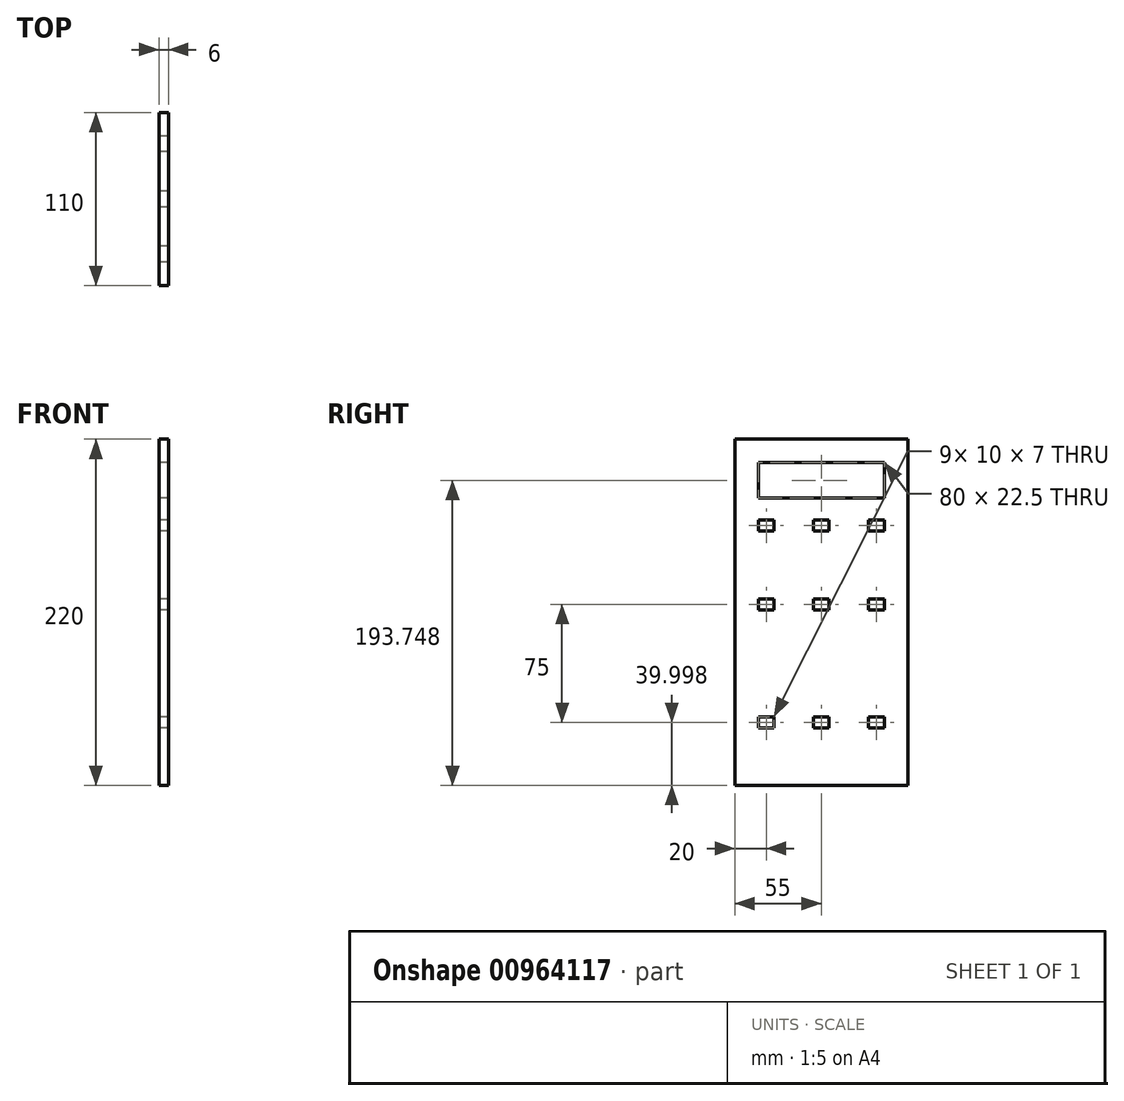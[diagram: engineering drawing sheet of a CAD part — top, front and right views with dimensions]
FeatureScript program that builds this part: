
annotation { "Feature Type Name" : "Feature", "Feature Type Description" : "" }
export const myFeature = defineFeature(function(context is Context, id is Id, definition is map)
    precondition{}
    {
        {
            var Q0;
            Q0=qCreatedBy(makeId("Right.planeOp"),FACE);
            var sketch = newSketch(context, id + "F0", { "sketchPlane" : qUnion([Q0])});
            skLineSegment(sketch, "E0.bottom", {"start": v(-47.5, 157.22) * mm, "end": v(62.5, 157.22) * mm});
            skLineSegment(sketch, "E0.top", {"start": v(-47.5, -62.78) * mm, "end": v(62.5, -62.78) * mm});
            skLineSegment(sketch, "E0.left", {"start": v(-47.5, 157.22) * mm, "end": v(-47.5, -62.78) * mm});
            skLineSegment(sketch, "E0.right", {"start": v(62.5, 157.22) * mm, "end": v(62.5, -62.78) * mm});
            skLineSegment(sketch, "E1.bottom", {"start": v(37.5, -19.28) * mm, "end": v(47.5, -19.28) * mm});
            skLineSegment(sketch, "E1.top", {"start": v(37.5, -26.28) * mm, "end": v(47.5, -26.28) * mm});
            skLineSegment(sketch, "E1.left", {"start": v(37.5, -19.28) * mm, "end": v(37.5, -26.28) * mm});
            skLineSegment(sketch, "E1.right", {"start": v(47.5, -19.28) * mm, "end": v(47.5, -26.28) * mm});
            skPoint(sketch, "E1.middle", {"position": v(42.5, -22.78) * mm});
            skLineSegment(sketch, "E2.bottom", {"start": v(2.5, -19.28) * mm, "end": v(12.5, -19.28) * mm});
            skLineSegment(sketch, "E2.top", {"start": v(2.5, -26.28) * mm, "end": v(12.5, -26.28) * mm});
            skLineSegment(sketch, "E2.left", {"start": v(2.5, -19.28) * mm, "end": v(2.5, -26.28) * mm});
            skLineSegment(sketch, "E2.right", {"start": v(12.5, -19.28) * mm, "end": v(12.5, -26.28) * mm});
            skPoint(sketch, "E2.middle", {"position": v(7.5, -22.78) * mm});
            skLineSegment(sketch, "E3.bottom", {"start": v(-22.5, -19.28) * mm, "end": v(-32.5, -19.28) * mm});
            skLineSegment(sketch, "E3.top", {"start": v(-22.5, -26.28) * mm, "end": v(-32.5, -26.28) * mm});
            skLineSegment(sketch, "E3.left", {"start": v(-22.5, -19.28) * mm, "end": v(-22.5, -26.28) * mm});
            skLineSegment(sketch, "E3.right", {"start": v(-32.5, -19.28) * mm, "end": v(-32.5, -26.28) * mm});
            skPoint(sketch, "E3.middle", {"position": v(-27.5, -22.78) * mm});
            skLineSegment(sketch, "E4", {"start": v(-27.5, -22.78) * mm, "end": v(42.5, -22.78) * mm});
            skLineSegment(sketch, "E5", {"start": v(-47.5, 130.37) * mm, "end": v(-32.5, 130.37) * mm});
            skLineSegment(sketch, "E6", {"start": v(62.5, 129.84) * mm, "end": v(47.5, 129.84) * mm});
            skLineSegment(sketch, "E7", {"start": v(9.43, 157.22) * mm, "end": v(9.43, 142.22) * mm});
            skLineSegment(sketch, "E8", {"start": v(9.43, 142.22) * mm, "end": v(-32.5, 142.22) * mm});
            skLineSegment(sketch, "E9", {"start": v(-32.5, 142.22) * mm, "end": v(-32.5, 119.72) * mm});
            skLineSegment(sketch, "E10", {"start": v(-32.5, 119.72) * mm, "end": v(47.5, 119.72) * mm});
            skLineSegment(sketch, "E11", {"start": v(47.5, 119.72) * mm, "end": v(47.5, 142.22) * mm});
            skLineSegment(sketch, "E12", {"start": v(47.5, 142.22) * mm, "end": v(9.43, 142.22) * mm});
            skLineSegment(sketch, "E13", {"start": v(30.25, -22.78) * mm, "end": v(30.25, 14.72) * mm});
            skLineSegment(sketch, "E14", {"start": v(30.25, 14.72) * mm, "end": v(-3.72, 14.72) * mm});
            skLineSegment(sketch, "E15.MirrorCS", {"start": v(37.5, 55.72) * mm, "end": v(47.5, 55.72) * mm});
            skLineSegment(sketch, "E16.MirrorCS", {"start": v(-32.5, 48.72) * mm, "end": v(-32.5, 55.72) * mm});
            skLineSegment(sketch, "E17.MirrorCS", {"start": v(37.5, 48.72) * mm, "end": v(37.5, 55.72) * mm});
            skLineSegment(sketch, "E18.MirrorCS", {"start": v(-22.5, 55.72) * mm, "end": v(-32.5, 55.72) * mm});
            skLineSegment(sketch, "E19.MirrorCS", {"start": v(2.5, 48.72) * mm, "end": v(2.5, 55.72) * mm});
            skLineSegment(sketch, "E20.MirrorCS", {"start": v(2.5, 55.72) * mm, "end": v(12.5, 55.72) * mm});
            skLineSegment(sketch, "E21.MirrorCS", {"start": v(37.5, 48.72) * mm, "end": v(47.5, 48.72) * mm});
            skLineSegment(sketch, "E22.MirrorCS", {"start": v(2.5, 48.72) * mm, "end": v(12.5, 48.72) * mm});
            skLineSegment(sketch, "E23.MirrorCS", {"start": v(-22.5, 48.72) * mm, "end": v(-22.5, 55.72) * mm});
            skLineSegment(sketch, "E24.MirrorCS", {"start": v(-22.5, 48.72) * mm, "end": v(-32.5, 48.72) * mm});
            skPoint(sketch, "E25.MirrorP", {"position": v(7.5, 52.22) * mm});
            skPoint(sketch, "E26.MirrorP", {"position": v(-27.5, 52.22) * mm});
            skPoint(sketch, "E27.MirrorP", {"position": v(42.5, 52.22) * mm});
            skLineSegment(sketch, "E28.MirrorCS", {"start": v(47.5, 48.72) * mm, "end": v(47.5, 55.72) * mm});
            skLineSegment(sketch, "E29.MirrorCS", {"start": v(-27.5, 52.22) * mm, "end": v(42.5, 52.22) * mm});
            skLineSegment(sketch, "E30.MirrorCS", {"start": v(12.5, 48.72) * mm, "end": v(12.5, 55.72) * mm});
            skLineSegment(sketch, "E31", {"start": v(24, 52.22) * mm, "end": v(24, 77.22) * mm});
            skLineSegment(sketch, "E32", {"start": v(24, 77.22) * mm, "end": v(-2.6, 77.22) * mm});
            skLineSegment(sketch, "E33.MirrorCS", {"start": v(-22.5, 98.72) * mm, "end": v(-32.5, 98.72) * mm});
            skLineSegment(sketch, "E34.MirrorCS", {"start": v(12.5, 105.72) * mm, "end": v(12.5, 98.72) * mm});
            skLineSegment(sketch, "E35.MirrorCS", {"start": v(37.5, 98.72) * mm, "end": v(47.5, 98.72) * mm});
            skLineSegment(sketch, "E36.MirrorCS", {"start": v(2.5, 98.72) * mm, "end": v(12.5, 98.72) * mm});
            skLineSegment(sketch, "E37.MirrorCS", {"start": v(2.5, 105.72) * mm, "end": v(12.5, 105.72) * mm});
            skLineSegment(sketch, "E38.MirrorCS", {"start": v(37.5, 105.72) * mm, "end": v(47.5, 105.72) * mm});
            skLineSegment(sketch, "E39.MirrorCS", {"start": v(-22.5, 105.72) * mm, "end": v(-22.5, 98.72) * mm});
            skPoint(sketch, "E40.MirrorP", {"position": v(42.5, 102.22) * mm});
            skLineSegment(sketch, "E41.MirrorCS", {"start": v(2.5, 105.72) * mm, "end": v(2.5, 98.72) * mm});
            skLineSegment(sketch, "E42.MirrorCS", {"start": v(47.5, 105.72) * mm, "end": v(47.5, 98.72) * mm});
            skLineSegment(sketch, "E43.MirrorCS", {"start": v(-32.5, 105.72) * mm, "end": v(-32.5, 98.72) * mm});
            skPoint(sketch, "E44.MirrorP", {"position": v(7.5, 102.22) * mm});
            skPoint(sketch, "E45.MirrorP", {"position": v(-27.5, 102.22) * mm});
            skLineSegment(sketch, "E46.MirrorCS", {"start": v(37.5, 105.72) * mm, "end": v(37.5, 98.72) * mm});
            skLineSegment(sketch, "E47.MirrorCS", {"start": v(-27.5, 102.22) * mm, "end": v(42.5, 102.22) * mm});
            skLineSegment(sketch, "E48.MirrorCS", {"start": v(-22.5, 105.72) * mm, "end": v(-32.5, 105.72) * mm});
            skSolve(sketch);
        }
        {
            var Q0;
            {var subQ1=sQuery(id+"F0.wireOp",EDGE,"E5");Q0=makeQuery(id+"F0.imprint","IMPRINT",FACE,{"disambiguationData":[TD([[makeQuery(id+"F0.imprint","IMPRINT",EDGE,{"derivedFrom":subQ1}),1.0]])]});}
            var Q1;
            {var subQ0=sQuery(id+"F0.wireOp",EDGE,"E6");Q1=makeQuery(id+"F0.imprint","IMPRINT",FACE,{"disambiguationData":[TD([[makeQuery(id+"F0.imprint","IMPRINT",EDGE,{"derivedFrom":subQ0}),-1.0]])]});}
            var Q2;
            {var subQ38=sQuery(id+"F0.wireOp",EDGE,"E0.top");Q2=makeQuery(id+"F0.imprint","IMPRINT",FACE,{"disambiguationData":[TD([[makeQuery(id+"F0.imprint","IMPRINT",EDGE,{"derivedFrom":subQ38}),1.0]])]});}
            extrude(context, id + "F1", {"entities" : qUnion([Q0, Q1, Q2]), "depth" : 6 * mm, "offsetDistance" : 25 * mm});
        }
    });
